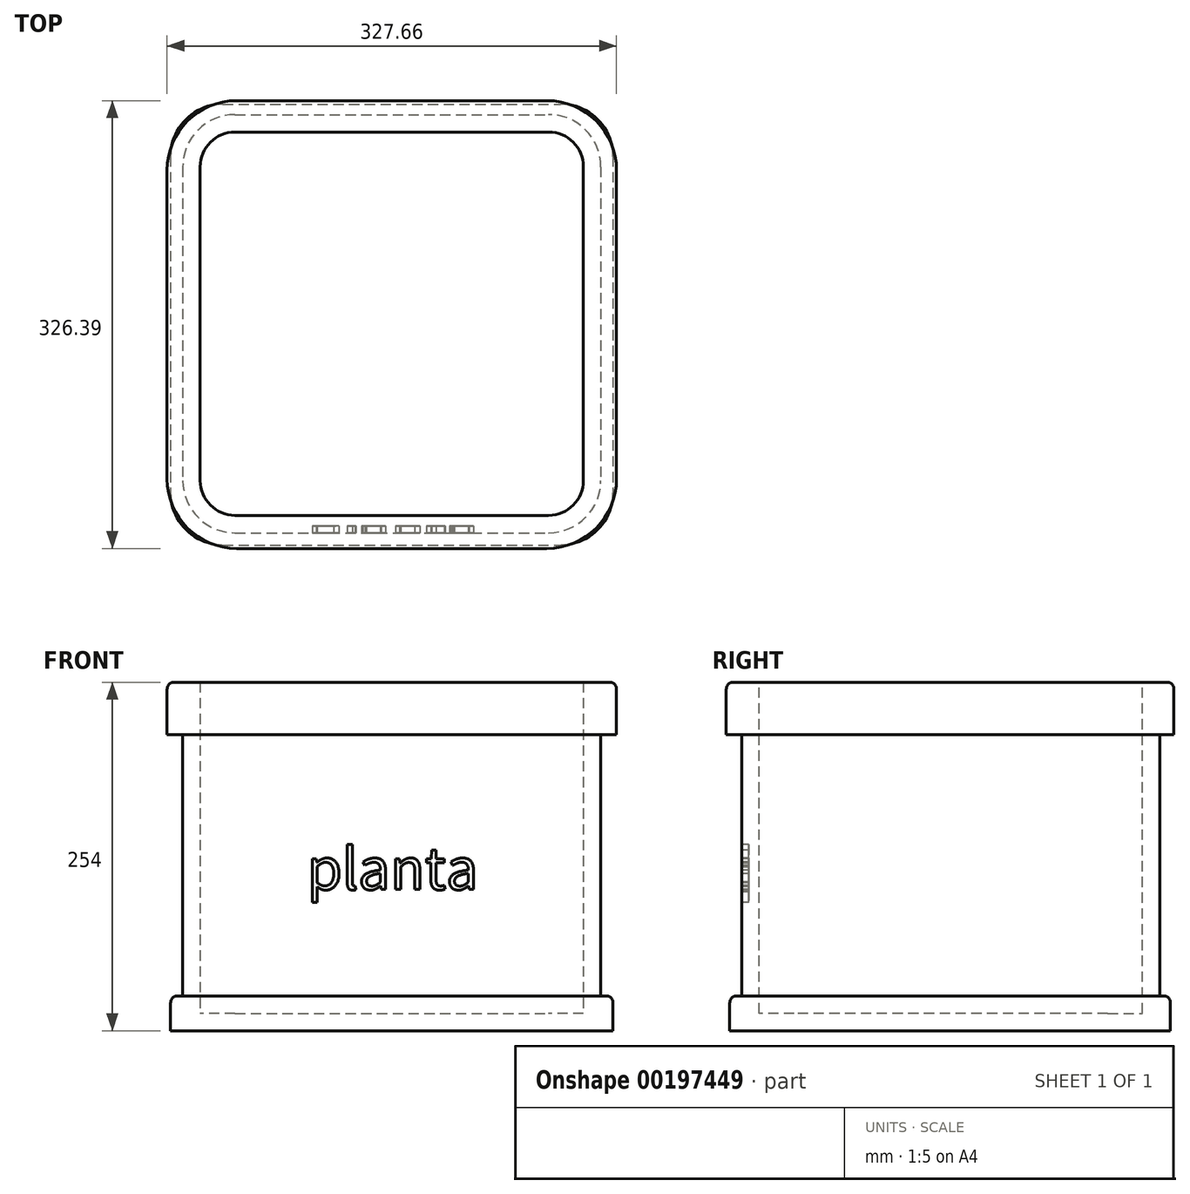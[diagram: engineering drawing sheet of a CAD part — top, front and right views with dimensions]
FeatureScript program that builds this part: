
annotation { "Feature Type Name" : "Feature", "Feature Type Description" : "" }
export const myFeature = defineFeature(function(context is Context, id is Id, definition is map)
    precondition{}
    {
        {
            var Q0;
            Q0=qCreatedBy(makeId("Top.planeOp"),FACE);
            var sketch = newSketch(context, id + "F0", { "sketchPlane" : qUnion([Q0])});
            skLineSegment(sketch, "E0.bottom", {"start": v(-122.4, 207.77) * mm, "end": v(106.2, 207.77) * mm});
            skLineSegment(sketch, "E0.top", {"start": v(-122.4, -97.03) * mm, "end": v(106.2, -97.03) * mm});
            skLineSegment(sketch, "E0.left", {"start": v(-160.5, 169.67) * mm, "end": v(-160.5, -58.93) * mm});
            skLineSegment(sketch, "E0.right", {"start": v(144.3, 169.67) * mm, "end": v(144.3, -58.93) * mm});
            skPoint(sketch, "E1.visualSharp", {"position": v(-160.5, 207.77) * mm});
            skArc(sketch, "E1.filletArc", {"start": v(-122.4, 207.77) * mm, "mid": v(-149.34, 196.61) * mm, "end": v(-160.5, 169.67) * mm});
            skPoint(sketch, "E2.visualSharp", {"position": v(144.3, 207.77) * mm});
            skArc(sketch, "E2.filletArc", {"start": v(144.3, 169.67) * mm, "mid": v(133.14, 196.61) * mm, "end": v(106.2, 207.77) * mm});
            skPoint(sketch, "E3.visualSharp", {"position": v(144.3, -97.03) * mm});
            skArc(sketch, "E3.filletArc", {"start": v(106.2, -97.03) * mm, "mid": v(133.14, -85.87) * mm, "end": v(144.3, -58.93) * mm});
            skPoint(sketch, "E4.visualSharp", {"position": v(-160.5, -97.03) * mm});
            skArc(sketch, "E4.filletArc", {"start": v(-160.5, -58.93) * mm, "mid": v(-149.34, -85.87) * mm, "end": v(-122.4, -97.03) * mm});
            skLineSegment(sketch, "E5.bottom", {"start": v(-131.3, 215.4) * mm, "end": v(115.09, 215.4) * mm});
            skLineSegment(sketch, "E5.top", {"start": v(-131.3, -105.92) * mm, "end": v(115.09, -105.92) * mm});
            skLineSegment(sketch, "E5.left", {"start": v(-169.4, 177.3) * mm, "end": v(-169.4, -67.82) * mm});
            skLineSegment(sketch, "E5.right", {"start": v(153.19, 177.3) * mm, "end": v(153.19, -67.82) * mm});
            skPoint(sketch, "E6.visualSharp", {"position": v(-169.4, -105.92) * mm});
            skArc(sketch, "E6.filletArc", {"start": v(-169.4, -67.82) * mm, "mid": v(-158.23, -94.76) * mm, "end": v(-131.3, -105.92) * mm});
            skPoint(sketch, "E7.visualSharp", {"position": v(-169.4, 215.4) * mm});
            skArc(sketch, "E7.filletArc", {"start": v(-131.3, 215.4) * mm, "mid": v(-158.23, 204.23) * mm, "end": v(-169.4, 177.3) * mm});
            skPoint(sketch, "E8.visualSharp", {"position": v(153.19, 215.4) * mm});
            skArc(sketch, "E8.filletArc", {"start": v(153.19, 177.3) * mm, "mid": v(142.03, 204.23) * mm, "end": v(115.09, 215.4) * mm});
            skPoint(sketch, "E9.visualSharp", {"position": v(153.19, -105.92) * mm});
            skArc(sketch, "E9.filletArc", {"start": v(115.09, -105.92) * mm, "mid": v(142.03, -94.76) * mm, "end": v(153.19, -67.82) * mm});
            skSolve(sketch);
        }
        {
            var Q0;
            Q0=makeQuery(id+"F0.imprint","IMPRINT",FACE,{"disambiguationData":[TD([[makeQuery(id+"F0.imprint","IMPRINT",EDGE,{"derivedFrom":sQuery(id+"F0.wireOp",EDGE,"E0.bottom")}),-1.0]])]});
            extrude(context, id + "F1", {"entities" : qUnion([Q0]), "depth" : 254 * mm});
        }
        {
            var Q0;
            Q0=makeQuery(id+"F1.opExtrude","CAP_FACE",FACE,{"disambiguationData":[OSD([sQuery(id+"F0.wireOp",EDGE,"E0.bottom"),sQuery(id+"F0.wireOp",EDGE,"E0.top"),sQuery(id+"F0.wireOp",EDGE,"E0.left"),sQuery(id+"F0.wireOp",EDGE,"E0.right"),sQuery(id+"F0.wireOp",EDGE,"E1.filletArc"),sQuery(id+"F0.wireOp",EDGE,"E2.filletArc"),sQuery(id+"F0.wireOp",EDGE,"E3.filletArc"),sQuery(id+"F0.wireOp",EDGE,"E4.filletArc")])],"isStart":false});
            shell(context, id + "F2", {"entities" : qUnion([Q0]), "thickness" : 12.7 * mm});
        }
        {
            var Q0;
            Q0=makeQuery(id+"F0.imprint","IMPRINT",FACE,{"disambiguationData":[TD([[makeQuery(id+"F0.imprint","IMPRINT",EDGE,{"derivedFrom":sQuery(id+"F0.wireOp",EDGE,"E0.bottom")}),1.0]])]});
            extrude(context, id + "F3", {"entities" : qUnion([Q0]), "operationType" : NewBodyOperationType.ADD, "depth" : 25.4 * mm});
        }
        {
            var Q0;
            Q0=makeQuery(id+"F1.opExtrude","CAP_FACE",FACE,{"disambiguationData":[OSD([sQuery(id+"F0.wireOp",EDGE,"E0.bottom"),sQuery(id+"F0.wireOp",EDGE,"E0.top"),sQuery(id+"F0.wireOp",EDGE,"E0.left"),sQuery(id+"F0.wireOp",EDGE,"E0.right"),sQuery(id+"F0.wireOp",EDGE,"E1.filletArc"),sQuery(id+"F0.wireOp",EDGE,"E2.filletArc"),sQuery(id+"F0.wireOp",EDGE,"E3.filletArc"),sQuery(id+"F0.wireOp",EDGE,"E4.filletArc")])],"isStart":false});
            var sketch = newSketch(context, id + "F4", { "sketchPlane" : qUnion([Q0])});
            skLineSegment(sketch, "E10.bottom", {"start": v(-121.13, 217.93) * mm, "end": v(104.93, 217.93) * mm});
            skLineSegment(sketch, "E10.top", {"start": v(-121.13, -108.46) * mm, "end": v(104.93, -108.46) * mm});
            skLineSegment(sketch, "E10.left", {"start": v(-171.93, 167.13) * mm, "end": v(-171.93, -57.66) * mm});
            skLineSegment(sketch, "E10.right", {"start": v(155.73, 167.13) * mm, "end": v(155.73, -57.66) * mm});
            skPoint(sketch, "E11.firstSnap0", {"position": v(-8.1, 207.77) * mm});
            skPoint(sketch, "E12.visualSharp", {"position": v(-171.93, 217.93) * mm});
            skArc(sketch, "E12.filletArc", {"start": v(-121.13, 217.93) * mm, "mid": v(-157.05, 203.05) * mm, "end": v(-171.93, 167.13) * mm});
            skPoint(sketch, "E13.visualSharp", {"position": v(155.73, 217.93) * mm});
            skArc(sketch, "E13.filletArc", {"start": v(155.73, 167.13) * mm, "mid": v(140.85, 203.05) * mm, "end": v(104.93, 217.93) * mm});
            skPoint(sketch, "E14.visualSharp", {"position": v(155.73, -108.46) * mm});
            skArc(sketch, "E14.filletArc", {"start": v(104.93, -108.46) * mm, "mid": v(140.85, -93.58) * mm, "end": v(155.73, -57.66) * mm});
            skPoint(sketch, "E15.visualSharp", {"position": v(-171.93, -108.46) * mm});
            skArc(sketch, "E15.filletArc", {"start": v(-171.93, -57.66) * mm, "mid": v(-157.05, -93.58) * mm, "end": v(-121.13, -108.46) * mm});
            skSolve(sketch);
        }
        {
            var Q0;
            Q0=makeQuery(id+"F4.imprint","IMPRINT",FACE,{"disambiguationData":[TD([[makeQuery(id+"F4.imprint","IMPRINT",EDGE,{"derivedFrom":sQuery(id+"F4.wireOp",EDGE,"E10.bottom")}),-1.0]])]});
            extrude(context, id + "F5", {"entities" : qUnion([Q0]), "operationType" : NewBodyOperationType.ADD, "oppositeDirection" : true, "depth" : 38.1 * mm});
        }
        {
            var Q0;
            Q0=makeQuery(id+"F1.opExtrude","SWEPT_FACE",FACE,{"disambiguationData":[OSD([sQuery(id+"F0.wireOp",EDGE,"E0.top")])]});
            var sketch = newSketch(context, id + "F6", { "sketchPlane" : qUnion([Q0])});
            skText(sketch, "E16", { "text": "planta", "fontName": "NotoSansCJKjp-Regular.otf"});
            const initialGuessF6  = {"E16": [-0.06998, 0.10292, 1, 0, 0.02974]};
            skSetInitialGuess(sketch, initialGuessF6);
            skSolve(sketch);
        }
        {
            var Q0;
            Q0 = qSketchRegion(id + "F6", true);
            extrude(context, id + "F7", {"entities" : qUnion([Q0]), "operationType" : NewBodyOperationType.REMOVE, "oppositeDirection" : true, "depth" : 5.08 * mm});
        }
        {
            var Q0;
            Q0=makeQuery(id+"F3.opExtrude","CAP_EDGE",EDGE,{"disambiguationData":[OSD([sQuery(id+"F0.wireOp",EDGE,"E5.top")])],"isStart":false});
            var Q1;
            Q1=makeQuery(id+"F3.opExtrude","CAP_EDGE",EDGE,{"disambiguationData":[OSD([sQuery(id+"F0.wireOp",EDGE,"E9.filletArc")])],"isStart":false});
            var Q2;
            Q2=makeQuery(id+"F3.opExtrude","CAP_EDGE",EDGE,{"disambiguationData":[OSD([sQuery(id+"F0.wireOp",EDGE,"E6.filletArc")])],"isStart":false});
            var Q3;
            Q3=makeQuery(id+"F3.opExtrude","CAP_EDGE",EDGE,{"disambiguationData":[OSD([sQuery(id+"F0.wireOp",EDGE,"E5.left")])],"isStart":false});
            var Q4;
            Q4=makeQuery(id+"F3.opExtrude","CAP_EDGE",EDGE,{"disambiguationData":[OSD([sQuery(id+"F0.wireOp",EDGE,"E5.right")])],"isStart":false});
            var Q5;
            Q5=makeQuery(id+"F3.opExtrude","CAP_EDGE",EDGE,{"disambiguationData":[OSD([sQuery(id+"F0.wireOp",EDGE,"E8.filletArc")])],"isStart":false});
            var Q6;
            Q6=makeQuery(id+"F3.opExtrude","CAP_EDGE",EDGE,{"disambiguationData":[OSD([sQuery(id+"F0.wireOp",EDGE,"E5.bottom")])],"isStart":false});
            var Q7;
            Q7=makeQuery(id+"F3.opExtrude","CAP_EDGE",EDGE,{"disambiguationData":[OSD([sQuery(id+"F0.wireOp",EDGE,"E7.filletArc")])],"isStart":false});
            fillet(context, id + "F8", {"entities" : qUnion([Q0, Q1, Q2, Q3, Q4, Q5, Q6, Q7]), "radius" : 5.08 * mm, "tangentPropagation" : true, "allowEdgeOverflow" : false});
        }
        {
            var Q0;
            Q0=makeQuery(id+"F5.opExtrude","CAP_EDGE",EDGE,{"disambiguationData":[OSD([sQuery(id+"F4.wireOp",EDGE,"E10.top")])],"isStart":true});
            var Q1;
            Q1=makeQuery(id+"F5.opExtrude","CAP_EDGE",EDGE,{"disambiguationData":[OSD([sQuery(id+"F4.wireOp",EDGE,"E15.filletArc")])],"isStart":true});
            var Q2;
            Q2=makeQuery(id+"F5.opExtrude","CAP_EDGE",EDGE,{"disambiguationData":[OSD([sQuery(id+"F4.wireOp",EDGE,"E10.left")])],"isStart":true});
            var Q3;
            Q3=makeQuery(id+"F5.opExtrude","CAP_EDGE",EDGE,{"disambiguationData":[OSD([sQuery(id+"F4.wireOp",EDGE,"E12.filletArc")])],"isStart":true});
            var Q4;
            Q4=makeQuery(id+"F5.opExtrude","CAP_EDGE",EDGE,{"disambiguationData":[OSD([sQuery(id+"F4.wireOp",EDGE,"E10.bottom")])],"isStart":true});
            var Q5;
            Q5=makeQuery(id+"F5.opExtrude","CAP_EDGE",EDGE,{"disambiguationData":[OSD([sQuery(id+"F4.wireOp",EDGE,"E13.filletArc")])],"isStart":true});
            var Q6;
            Q6=makeQuery(id+"F5.opExtrude","CAP_EDGE",EDGE,{"disambiguationData":[OSD([sQuery(id+"F4.wireOp",EDGE,"E10.right")])],"isStart":true});
            var Q7;
            Q7=makeQuery(id+"F5.opExtrude","CAP_EDGE",EDGE,{"disambiguationData":[OSD([sQuery(id+"F4.wireOp",EDGE,"E14.filletArc")])],"isStart":true});
            fillet(context, id + "F9", {"entities" : qUnion([Q0, Q1, Q2, Q3, Q4, Q5, Q6, Q7]), "radius" : 5.08 * mm, "tangentPropagation" : true, "allowEdgeOverflow" : false});
        }
    });
